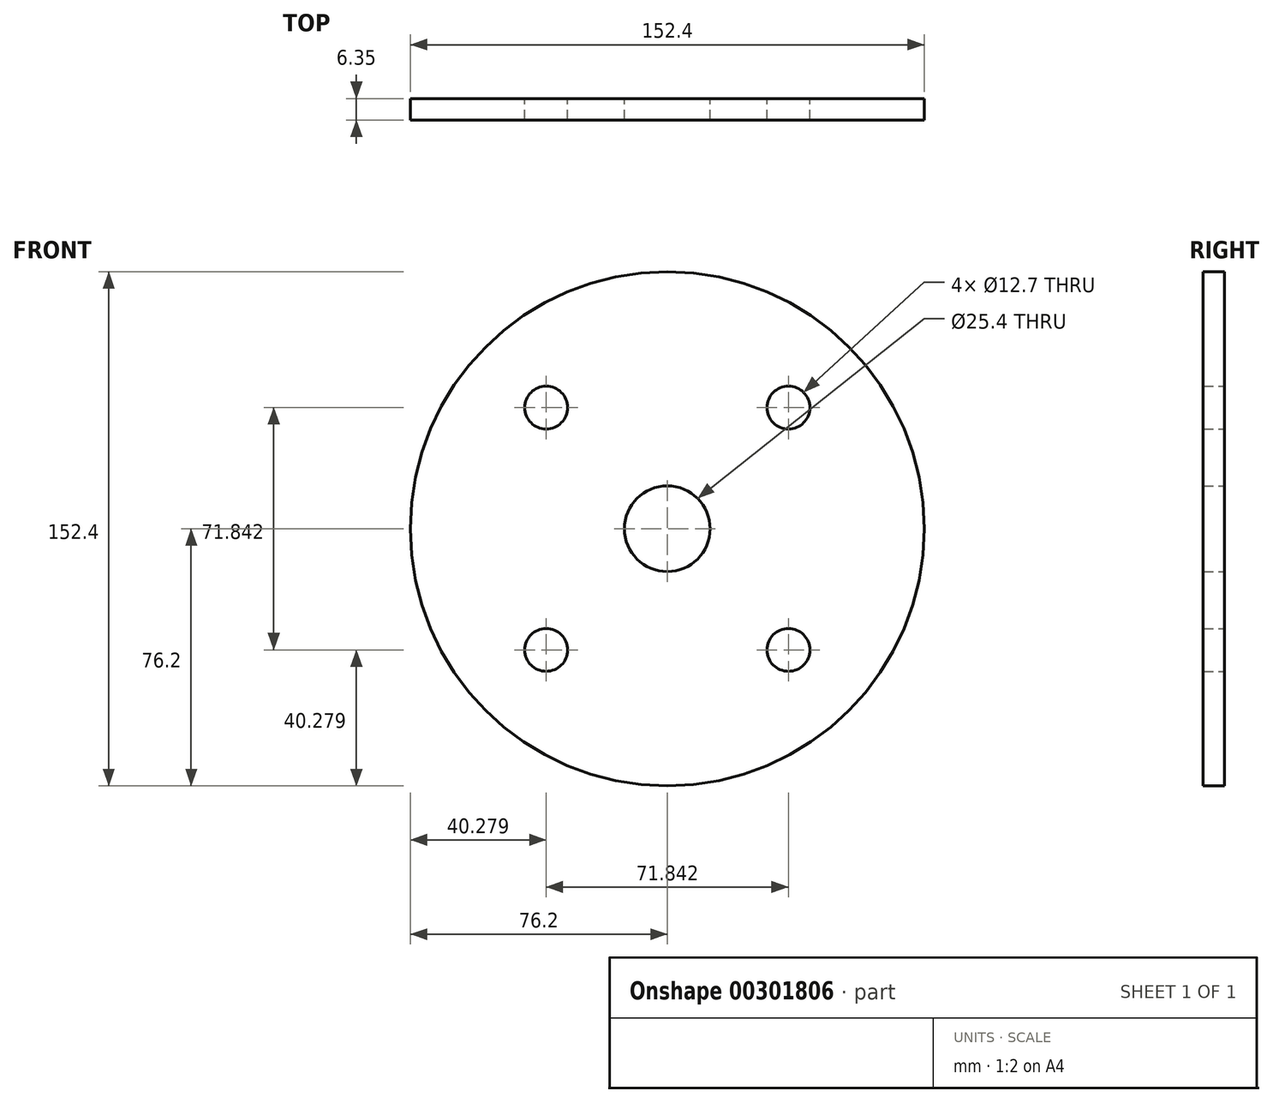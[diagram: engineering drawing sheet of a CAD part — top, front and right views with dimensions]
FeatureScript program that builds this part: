
annotation { "Feature Type Name" : "Feature", "Feature Type Description" : "" }
export const myFeature = defineFeature(function(context is Context, id is Id, definition is map)
    precondition{}
    {
        {
            var Q0;
            Q0=qCreatedBy(makeId("Front.planeOp"),FACE);
            var sketch = newSketch(context, id + "F0", { "sketchPlane" : qUnion([Q0])});
            skCircle(sketch, "E0", {"center": v(0, 0) * mm, "radius": 12.7 * mm});
            skCircle(sketch, "E1", {"center": v(0, 0) * mm, "radius": 76.2 * mm});
            skCircle(sketch, "E2", {"center": v(-35.92, 35.92) * mm, "radius": 6.35 * mm});
            skLineSegment(sketch, "E3", {"start": v(0, -83.55) * mm, "end": v(0, 69.02) * mm, "construction": true});
            skLineSegment(sketch, "E4", {"start": v(87.45, 0) * mm, "end": v(-118.93, 0) * mm, "construction": true});
            skCircle(sketch, "E5.MirrorC", {"center": v(35.92, 35.92) * mm, "radius": 6.35 * mm});
            skCircle(sketch, "E6.MirrorC", {"center": v(-35.92, -35.92) * mm, "radius": 6.35 * mm});
            skCircle(sketch, "E7.MirrorC", {"center": v(35.92, -35.92) * mm, "radius": 6.35 * mm});
            skLineSegment(sketch, "E8", {"start": v(0, 0) * mm, "end": v(-35.92, 35.92) * mm, "construction": true});
            skSolve(sketch);
        }
        {
            var Q0;
            Q0=makeQuery(id+"F0.imprint","IMPRINT",FACE,{"disambiguationData":[TD([[makeQuery(id+"F0.imprint","IMPRINT",EDGE,{"derivedFrom":sQuery(id+"F0.wireOp",EDGE,"E0")}),-1.0]])]});
            extrude(context, id + "F1", {"entities" : qUnion([Q0]), "depth" : 6.35 * mm});
        }
    });
